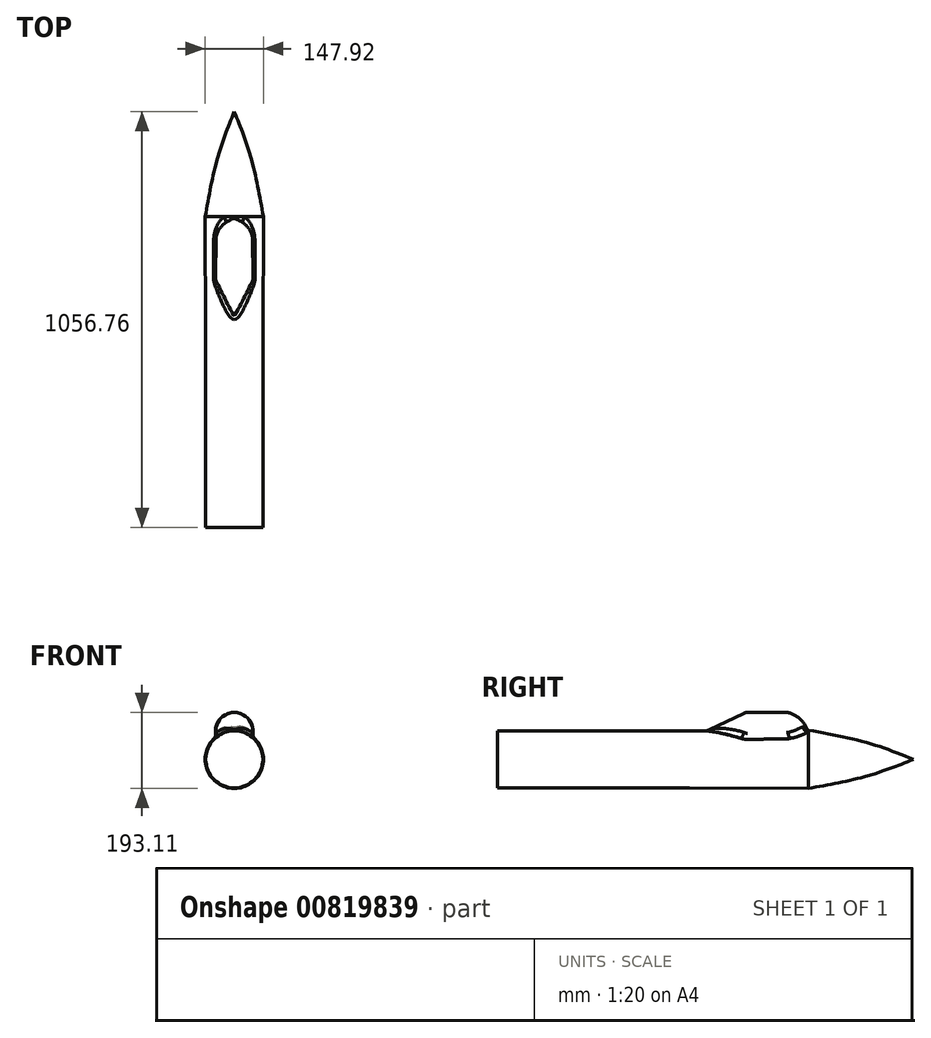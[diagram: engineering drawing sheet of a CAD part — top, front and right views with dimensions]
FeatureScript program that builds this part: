
annotation { "Feature Type Name" : "Feature", "Feature Type Description" : "" }
export const myFeature = defineFeature(function(context is Context, id is Id, definition is map)
    precondition{}
    {
        {
            var Q0;
            Q0=qCreatedBy(makeId("Right.planeOp"),FACE);
            var sketch = newSketch(context, id + "F0", { "sketchPlane" : qUnion([Q0])});
            skFitSpline(sketch, "E0", {"points": [v(159.68, 54.07) * mm, v(306.71, 23.06) * mm, v(426.9, -19.9) * mm], "startDerivative": vector(290.85, -51.78) * mm, "endDerivative": vector(242.94, -96.75) * mm});
            skLineSegment(sketch, "E1", {"start": v(426.9, -19.9) * mm, "end": v(-141.86, -19.9) * mm});
            skLineSegment(sketch, "E2", {"start": v(-141.86, -19.9) * mm, "end": v(-141.86, 52.52) * mm});
            skLineSegment(sketch, "E3", {"start": v(-141.86, 52.52) * mm, "end": v(159.68, 54.07) * mm});
            skSolve(sketch);
        }
        {
            var Q0;
            Q0=makeQuery(id+"F0.imprint","IMPRINT",FACE,{"disambiguationData":[TD([[makeQuery(id+"F0.imprint","IMPRINT",EDGE,{"derivedFrom":sQuery(id+"F0.wireOp",EDGE,"E0")}),-1.0]])]});
            var Q1;
            Q1=sQuery(id+"F0.wireOp",EDGE,"E1");
            revolve(context, id + "F1", {"surfaceOperationType" : NewSurfaceOperationType.NEW, "entities" : qUnion([Q0]), "axis" : qUnion([Q1]), "revolveType" : RevolveType.FULL});
        }
        {
            var Q0;
            Q0=qCreatedBy(makeId("Right.planeOp"),FACE);
            var sketch = newSketch(context, id + "F2", { "sketchPlane" : qUnion([Q0])});
            skArc(sketch, "E4", {"start": v(157.77, 53.14) * mm, "mid": v(137.75, 83.44) * mm, "end": v(105.06, 99.26) * mm});
            skLineSegment(sketch, "E5", {"start": v(105.06, 99.26) * mm, "end": v(0, 99.26) * mm});
            skLineSegment(sketch, "E6", {"start": v(0, 99.26) * mm, "end": v(-102.08, 50.23) * mm});
            skLineSegment(sketch, "E7", {"start": v(-102.08, 50.23) * mm, "end": v(157.77, 53.14) * mm});
            skSolve(sketch);
        }
        {
            var Q0;
            Q0 = qSketchRegion(id + "F2", true);
            var Q1;
            Q1=sQuery(id+"F2.wireOp",EDGE,"E7");
            revolve(context, id + "F3", {"operationType" : NewBodyOperationType.ADD, "surfaceOperationType" : NewSurfaceOperationType.NEW, "entities" : qUnion([Q0]), "axis" : qUnion([Q1]), "revolveType" : RevolveType.FULL});
        }
        {
            var Q0;
            Q0=makeQuery(id+"F3.boolean.opBoolean","INTERSECT",EDGE,{"disambiguationData":[OD(1.0)],"derivedFrom":[makeQuery(id+"F1.opRevolve","SWEPT_FACE",FACE,{"disambiguationData":[OSD([sQuery(id+"F0.wireOp",EDGE,"E3")])]}),makeQuery(id+"F3.opRevolve","SWEPT_FACE",FACE,{"disambiguationData":[OSD([sQuery(id+"F2.wireOp",EDGE,"E5")])]})]});
            var Q1;
            Q1=makeQuery(id+"F3.boolean.opBoolean","INTERSECT",EDGE,{"derivedFrom":[makeQuery(id+"F1.opRevolve","SWEPT_FACE",FACE,{"disambiguationData":[OSD([sQuery(id+"F0.wireOp",EDGE,"E3")])]}),makeQuery(id+"F3.opRevolve","SWEPT_FACE",FACE,{"disambiguationData":[OSD([sQuery(id+"F2.wireOp",EDGE,"E4")])]})]});
            var Q2;
            Q2=makeQuery(id+"F3.boolean.opBoolean","INTERSECT",EDGE,{"disambiguationData":[OD(0.0)],"derivedFrom":[makeQuery(id+"F1.opRevolve","SWEPT_FACE",FACE,{"disambiguationData":[OSD([sQuery(id+"F0.wireOp",EDGE,"E3")])]}),makeQuery(id+"F3.opRevolve","SWEPT_FACE",FACE,{"disambiguationData":[OSD([sQuery(id+"F2.wireOp",EDGE,"E5")])]})]});
            var Q3;
            Q3=makeQuery(id+"F3.boolean.opBoolean","INTERSECT",EDGE,{"derivedFrom":[makeQuery(id+"F1.opRevolve","SWEPT_FACE",FACE,{"disambiguationData":[OSD([sQuery(id+"F0.wireOp",EDGE,"E3")])]}),makeQuery(id+"F3.opRevolve","SWEPT_FACE",FACE,{"disambiguationData":[OSD([sQuery(id+"F2.wireOp",EDGE,"E6")])]})]});
            var Q4;
            Q4=makeQuery(id+"F3.opRevolve","SWEPT_EDGE",EDGE,{"disambiguationData":[OSD([sQuery(id+"F2.wireOp",EDGE,"E5"),sQuery(id+"F2.wireOp",EDGE,"E6")])]});
            var Q5;
            Q5=makeQuery(id+"F3.opRevolve","SWEPT_EDGE",EDGE,{"disambiguationData":[OSD([sQuery(id+"F2.wireOp",EDGE,"E4"),sQuery(id+"F2.wireOp",EDGE,"E5")])]});
            fillet(context, id + "F4", {"entities" : qUnion([Q0, Q1, Q2, Q3, Q4, Q5]), "radius" : 19.44 * mm, "tangentPropagation" : true, "allowEdgeOverflow" : false});
        }
        {
            var Q0;
            Q0=makeQuery(id+"F1.opRevolve","SWEPT_FACE",FACE,{"disambiguationData":[OSD([sQuery(id+"F0.wireOp",EDGE,"E2")])]});
            var sketch = newSketch(context, id + "F5", { "sketchPlane" : qUnion([Q0])});
            skSolve(sketch);
        }
        {
            var Q0;
            Q0=makeQuery(id+"F5.imprint","IMPRINT",FACE,{"disambiguationData":[TD([[makeQuery(id+"F5.imprint","IMPRINT",EDGE,{"derivedFrom":makeQuery(id+"F1.opRevolve","SWEPT_EDGE",EDGE,{"disambiguationData":[OSD([sQuery(id+"F0.wireOp",EDGE,"E2"),sQuery(id+"F0.wireOp",EDGE,"E3")])]})}),-1.0]])]});
            extrude(context, id + "F6", {"entities" : qUnion([Q0]), "operationType" : NewBodyOperationType.ADD, "depth" : 488 * mm, "offsetDistance" : 25.4 * mm});
        }
    });
